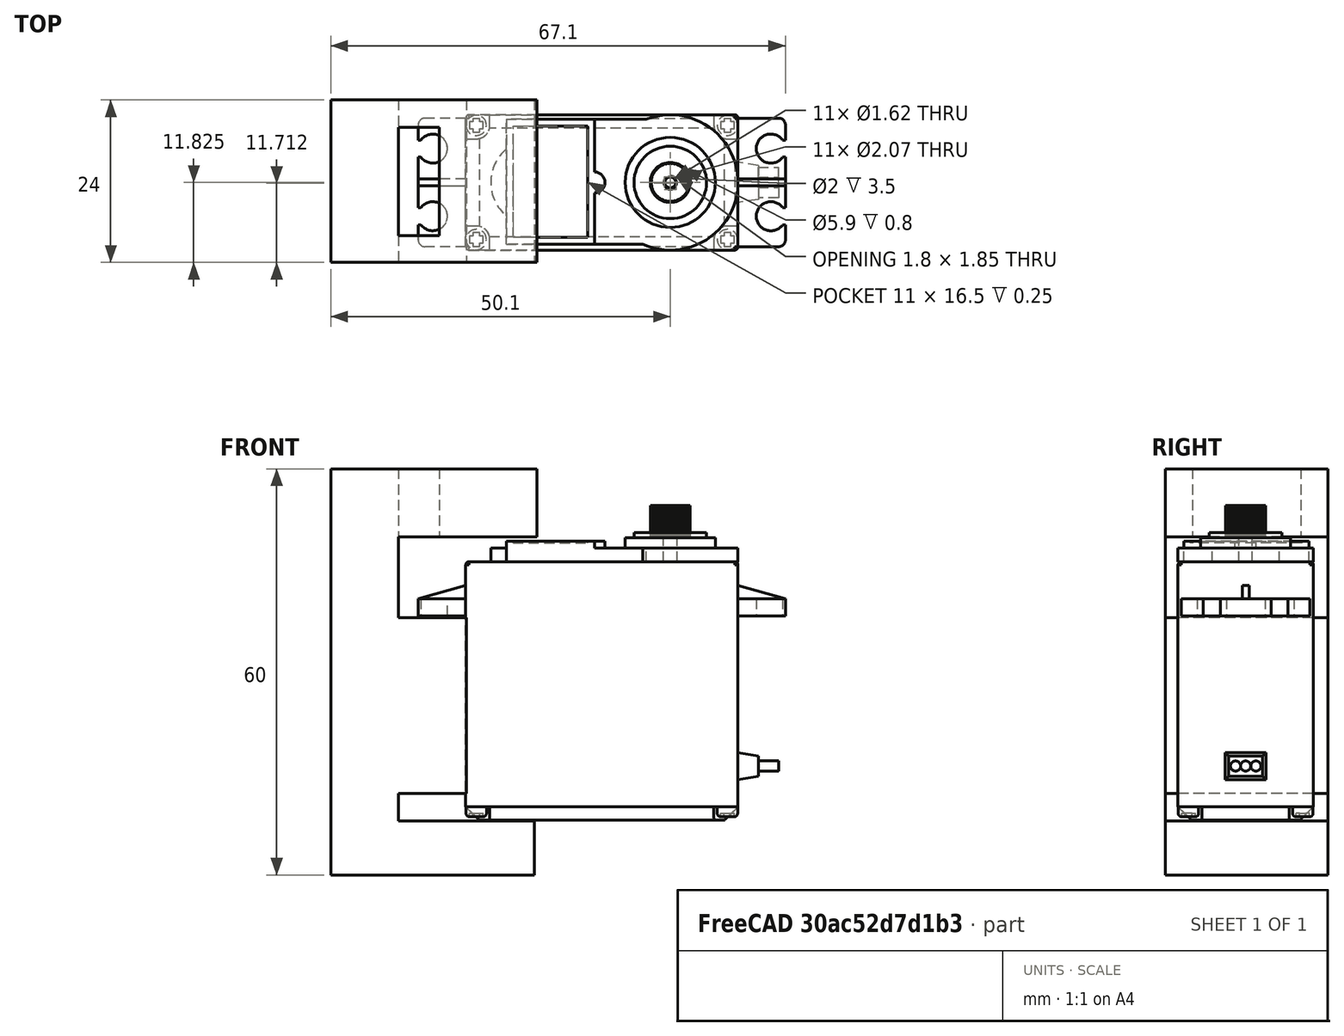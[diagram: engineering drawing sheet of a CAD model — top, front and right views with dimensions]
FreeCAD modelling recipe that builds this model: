
FCSTD DOCUMENT  (FreeCAD 0.21R33771 (Git))
Label: U_Servo_angulo_v3
License: All rights reserved
LicenseURL: http://en.wikipedia.org/wiki/All_rights_reserved
objects: Sketcher::SketchObject×3, Mesh::Feature×1, Part::Feature×1, PartDesign::Pad×1, PartDesign::Pocket×1, PartDesign::Body×1
note: 9 computed .brp shape members not serialized (recipe doc carries the construction recipe); baked Part::Feature solids carry a one-line shape summary decoded from their .brp

FEATURE [Mesh::Feature] servo_lower_cover_fake_shaft
  Placement = pos=(0,-12,2) rot=(0,1,0;3.14159rad)
FEATURE [Part::Feature] Part__Feature  label="MG996R"
  Placement = pos=(0,-9,-0.5) rot=(0,0,1;0rad)
  shape: bbox 54.21 x 20.13 x 46.64 mm, 453 faces, 11 solids (baked)
FEATURE [Sketcher::SketchObject] Sketch
  FullyConstrained = false
  MapMode = 5
  Placement = pos=(0,0,0) rot=(1,0,0;1.5708rad)
  Support = -> [XZ_Plane]
  sketch-geometry (12):
    g0: LineSegment StartX=-9.57792 StartY=39.9337 StartZ=0 EndX=-30 EndY=39.9337 EndZ=0
    g1: LineSegment StartX=-9.57792 StartY=50 StartZ=0 EndX=-40 EndY=50 EndZ=0
    g2: LineSegment StartX=-20 StartY=28 StartZ=0 EndX=-30 EndY=28 EndZ=0
    g3: LineSegment StartX=-20 StartY=2.0296 StartZ=0 EndX=-30 EndY=2.0296 EndZ=0
    g4: LineSegment StartX=-40 StartY=-10 StartZ=0 EndX=-9.99258 EndY=-10 EndZ=0
    g5: LineSegment StartX=-9.99258 StartY=-2 StartZ=0 EndX=-30 EndY=-2 EndZ=0
    g6: LineSegment StartX=-40 StartY=50 StartZ=0 EndX=-40 EndY=-10 EndZ=0
    g7: LineSegment StartX=-9.99258 StartY=-10 StartZ=0 EndX=-9.99258 EndY=-2 EndZ=0
    g8: LineSegment StartX=-30 StartY=-2 StartZ=0 EndX=-30 EndY=2.0296 EndZ=0
    g9: LineSegment StartX=-20 StartY=28 StartZ=0 EndX=-20 EndY=2.0296 EndZ=0
    g10: LineSegment StartX=-30 StartY=28 StartZ=0 EndX=-30 EndY=39.9337 EndZ=0
    g11: LineSegment StartX=-9.57792 StartY=39.9337 StartZ=0 EndX=-9.57792 EndY=50 EndZ=0
  constraints (24):
    c: Horizontal(g0)
    c: Horizontal(g1)
    c: Horizontal(g2)
    c: Horizontal(g3)
    c: Horizontal(g4)
    c: Horizontal(g5)
    c: Coincident(g6,g1)
    c: Coincident(g6,g4)
    c: Vertical(g6)
    c: Coincident(g7,g4)
    c: Coincident(g7,g5)
    c: Vertical(g7)
    c: Coincident(g8,g5)
    c: Coincident(g8,g3)
    c: Vertical(g8)
    c: Coincident(g9,g2)
    c: Coincident(g9,g3)
    c: Vertical(g9)
    c: Coincident(g10,g2)
    c: Coincident(g10,g0)
    c: Vertical(g10)
    c: Coincident(g11,g0)
    c: Coincident(g11,g1)
    c: Vertical(g11)
FEATURE [PartDesign::Pad] Pad
  Direction = (0,-1,-2e-16)
  Length = 24
  Length2 = 10
  Placement = pos=(0,0,0) rot=(1,0,0;1.5708rad)
  Profile = -> Sketch
  ReferenceAxis = -> Sketch [N_Axis]
  Type = 0
FEATURE [Sketcher::SketchObject] Sketch001
  FullyConstrained = false
  MapMode = 5
  Placement = pos=(0,-1.11e-14,50) rot=(0,0,1;3.14159rad)
  Support = -> [Pad]
  sketch-geometry (4):
    g0: LineSegment StartX=24 StartY=20.048 StartZ=0 EndX=30 EndY=20.048 EndZ=0
    g1: LineSegment StartX=30 StartY=20.048 StartZ=0 EndX=30 EndY=4.04802 EndZ=0
    g2: LineSegment StartX=30 StartY=4.04802 StartZ=0 EndX=24 EndY=4.04802 EndZ=0
    g3: LineSegment StartX=24 StartY=4.04802 StartZ=0 EndX=24 EndY=20.048 EndZ=0
  constraints (8):
    c: Coincident(g0,g1)
    c: Coincident(g1,g2)
    c: Coincident(g2,g3)
    c: Coincident(g3,g0)
    c: Horizontal(g0)
    c: Horizontal(g2)
    c: Vertical(g1)
    c: Vertical(g3)
FEATURE [PartDesign::Pocket] Pocket
  BaseFeature = -> Pad
  Direction = (0,2e-16,-1)
  Length = 11
  Length2 = 5
  Placement = pos=(0,0,0) rot=(1,0,0;1.5708rad)
  Profile = -> Sketch001
  ReferenceAxis = -> Sketch001 [N_Axis]
  Type = 0
FEATURE [Sketcher::SketchObject] Sketch003
  FullyConstrained = false
  MapMode = 5
  Placement = pos=(0,0,0) rot=(1,0,0;1.5708rad)
  Support = -> [XZ_Plane]
  sketch-geometry (10):
    g0: LineSegment StartX=0.057249 StartY=41.3 StartZ=0 EndX=50 EndY=41.3 EndZ=0
    g1: LineSegment StartX=0.057249 StartY=41.3 StartZ=0 EndX=0.057249 EndY=45.6457 EndZ=0
    g2: LineSegment StartX=0 StartY=-4 StartZ=0 EndX=0 EndY=-10 EndZ=0
    g3: LineSegment StartX=0 StartY=-10 StartZ=0 EndX=55 EndY=-10 EndZ=0
    g4: LineSegment StartX=50 StartY=41.3 StartZ=0 EndX=50 EndY=-4 EndZ=0
    g5: LineSegment StartX=55 StartY=49.6 StartZ=0 EndX=25.0708 EndY=49.6 EndZ=0
    g6: LineSegment StartX=25.0708 StartY=49.6 StartZ=0 EndX=25.0708 EndY=45.6457 EndZ=0
    g7: LineSegment StartX=0.057249 StartY=45.6457 StartZ=0 EndX=25.0708 EndY=45.6457 EndZ=0
    g8: LineSegment StartX=55 StartY=49.6 StartZ=0 EndX=55 EndY=-10 EndZ=0
    g9: LineSegment StartX=0 StartY=-4 StartZ=0 EndX=50 EndY=-4 EndZ=0
  constraints (20):
    c: Horizontal(g0)
    c: Coincident(g1,g0)
    c: Vertical(g1)
    c: Vertical(g2)
    c: Coincident(g3,g2)
    c: Horizontal(g3)
    c: Coincident(g4,g0)
    c: Vertical(g4)
    c: Horizontal(g5)
    c: Coincident(g6,g5)
    c: Vertical(g6)
    c: Coincident(g7,g1)
    c: Coincident(g7,g6)
    c: Horizontal(g7)
    c: Coincident(g8,g5)
    c: Coincident(g8,g3)
    c: Vertical(g8)
    c: Coincident(g9,g2)
    c: Coincident(g9,g4)
    c: Horizontal(g9)
FEATURE [PartDesign::Body] Body
  Group = -> [Sketch,Pad,Sketch001,Pocket,Sketch003]
  Origin = -> Origin
  Tip = -> Pocket
